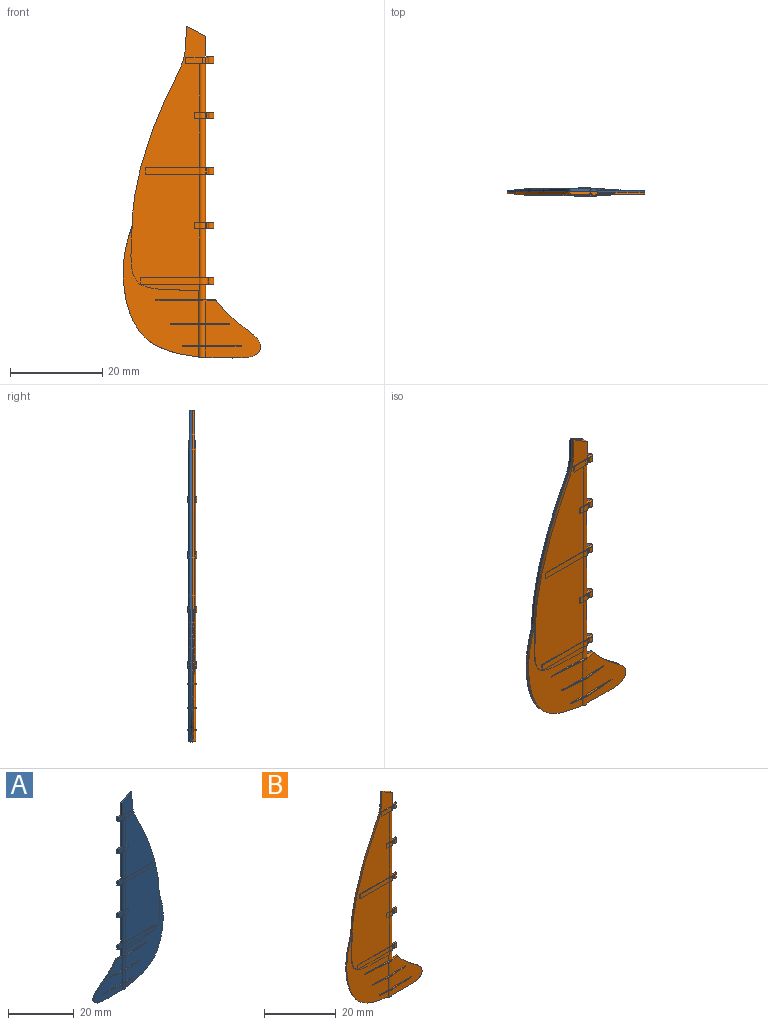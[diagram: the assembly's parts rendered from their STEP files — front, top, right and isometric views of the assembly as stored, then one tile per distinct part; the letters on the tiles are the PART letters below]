
ASSEMBLY  parts=2 mates=1
PART A: 77 faces, bbox 30.6x1x72.1 mm
  f0: plane 4.5x0.6mm, normal (-1,0,0), area 2.7mm2, adj f7,f12,f39,f73
  f1: plane 28.83x17.51mm, normal (0,-1,0), area 202.8mm2, adj f2,f4,f8,f10,f11,f13,f16,f17
  f2: cylinder r=0.79mm len=2.28mm, axis (0,0,1), area 3.8mm2, adj f1,f3,f11,f12,f14,f67
  f3: plane 13.22x13.04mm, normal (0,-1,0), area 99mm2, adj f2,f4,f13,f14,f15,f17,f18,f62
  f4: cylinder r=0.79mm len=4.59mm, axis (0,0,1), area 7.5mm2, adj f1,f3,f62,f68
  f5: cylinder r=0.99mm len=1.4mm, axis (0,0,1), area 2.1mm2, adj f46,f47,f50,f59
  f6: cylinder r=0.99mm len=1.4mm, axis (0,0,1), area 2.1mm2, adj f48,f49,f54,f56
  f7: plane 57.26x16.41mm, normal (0,-1,0), area 557.2mm2, adj f0,f8,f9,f10,f21,f27,f30,f31
  f8: cylinder r=0.79mm len=3.37mm, axis (0,0,1), area 6.6mm2, adj f1,f7,f10,f12,f16,f21
  f9: plane 15.77x0.99mm, normal (0,0,1), area 4mm2, adj f7,f12,f22,f23,f24,f25,f26,f27
  f10: extruded ~14.86x14mm, area 5.2mm2, adj f1,f7,f8,f40
  f11: extruded ~28.36x16.35mm, area 15.2mm2, adj f1,f2,f12,f40
  f12: plane 72.1x30.59mm, normal (0,1,0), area 1005.3mm2, adj f0,f2,f8,f9,f11,f14,f15,f16
  f13: cylinder r=0.79mm len=4.99mm, axis (0,0,1), area 8.1mm2, adj f1,f3,f17,f63
  f14: plane 1.46x0.79mm, normal (0,0,-1), area 0.8mm2, adj f2,f3,f12,f15
  f15: extruded ~12.61x12.32mm, area 11.2mm2, adj f3,f12,f14,f16
  f16: plane 12.82x0.99mm, normal (0,0,1), area 4.3mm2, adj f1,f8,f12,f15,f18,f19,f20
  f17: plane 12.82x0.59mm, normal (0,0,-1), area 3.4mm2, adj f1,f3,f13,f18,f19,f20
  f18: plane 2.67x0.57mm, normal (-0.21,-0.98,0), area 0.5mm2, adj f3,f16,f17,f19
  f19: cylinder r=0.99mm len=0.26mm, axis (0,0,1), area 0.1mm2, adj f16,f17,f18,f20
  f20: plane 9.89x0.59mm, normal (0.06,-1,0), area 2mm2, adj f1,f16,f17,f19
  f21: plane 15.77x0.99mm, normal (0,0,-1), area 4mm2, adj f7,f8,f12,f22,f23,f24,f25,f26
  f22: plane 1.4x0.01mm, normal (1,0,0), area 0mm2, adj f9,f21,f23,f25
  f23: plane 1.4x0.47mm, normal (0,-1,0), area 0.7mm2, adj f9,f21,f22,f24
  f24: cylinder r=0.79mm len=1.4mm, axis (0,0,1), area 2.5mm2, adj f9,f12,f21,f23
  f25: cylinder r=0.99mm len=1.4mm, axis (0,0,1), area 2.1mm2, adj f9,f21,f22,f26
  f26: plane 12.64x1.4mm, normal (0,-1,0), area 17.7mm2, adj f9,f21,f25,f27
  f27: plane 1.4x0.2mm, normal (1,0,0), area 0.3mm2, adj f7,f9,f21,f26
  f28: plane 1.4x0.01mm, normal (1,0,0), area 0mm2, adj f29,f30,f31,f33
  f29: plane 1.4x0.47mm, normal (0,-1,0), area 0.7mm2, adj f28,f30,f31,f32
  f30: plane 4.25x0.99mm, normal (0,0,1), area 1.7mm2, adj f7,f12,f28,f29,f32,f33,f35,f52
  f31: plane 4.25x0.99mm, normal (0,0,-1), area 1.7mm2, adj f7,f12,f28,f29,f32,f33,f36,f52
  f32: cylinder r=0.79mm len=1.4mm, axis (0,0,-1), area 2.5mm2, adj f12,f29,f30,f31
  f33: cylinder r=0.99mm len=1.4mm, axis (0,0,1), area 2.1mm2, adj f28,f30,f31,f52
  f34: cylinder r=0.79mm len=10.59mm, axis (0,0,1), area 19mm2, adj f7,f12,f47,f48
  f35: cylinder r=0.79mm len=10.44mm, axis (0,0,1), area 18.7mm2, adj f7,f12,f30,f46
  f36: cylinder r=0.79mm len=10.58mm, axis (0,0,1), area 18.9mm2, adj f7,f9,f12,f31
  f37: cylinder r=0.79mm len=10.57mm, axis (0,0,1), area 18.9mm2, adj f7,f12,f38,f41,f43,f49
  f38: plane 2.56x0.8mm, normal (0,0,-1), area 1.2mm2, adj f12,f37,f41,f45,f72,f75,f76
  f39: plane 4.12x2.22mm, normal (-0.47,0,0.88), area 2.8mm2, adj f0,f7,f12,f40
  f40: extruded ~43.25x11.74mm, area 27.2mm2, adj f7,f10,f11,f12,f39
  f41: plane 0.01x0.01mm, normal (-1,0,0), area 0mm2, adj f37,f38,f43,f45
  f42: plane 4.3x0.2mm, normal (0,0,1), area 0.8mm2, adj f7,f44,f45,f76
  f43: plane 3.54x0.2mm, normal (0,0,-1), area 0.6mm2, adj f7,f37,f41,f44,f45
  f44: plane 1.4x0.2mm, normal (1,0,0), area 0.3mm2, adj f7,f42,f43,f45
  f45: plane 3.64x1.4mm, normal (0,-1,0), area 5.1mm2, adj f38,f41,f42,f43,f44,f76
  f46: plane 14.77x0.99mm, normal (0,0,-1), area 3.8mm2, adj f5,f7,f12,f35,f50,f51,f59,f60
  f47: plane 14.77x0.99mm, normal (0,0,1), area 3.8mm2, adj f5,f7,f12,f34,f50,f51,f59,f60
  f48: plane 4.27x0.99mm, normal (0,0,-1), area 1.7mm2, adj f6,f7,f12,f34,f54,f55,f56,f57
  f49: plane 4.27x0.99mm, normal (0,0,1), area 1.7mm2, adj f6,f7,f12,f37,f54,f55,f56,f57
  f50: plane 11.63x1.4mm, normal (0,-1,0), area 16.3mm2, adj f5,f46,f47,f51
  f51: plane 1.4x0.2mm, normal (1,0,0), area 0.3mm2, adj f7,f46,f47,f50
  f52: plane 1.4x1.11mm, normal (0,-1,0), area 1.6mm2, adj f30,f31,f33,f53
  f53: plane 1.4x0.2mm, normal (1,0,0), area 0.3mm2, adj f7,f30,f31,f52
  f54: plane 1.4x1.13mm, normal (0,-1,0), area 1.6mm2, adj f6,f48,f49,f55
  f55: plane 1.4x0.2mm, normal (1,0,0), area 0.3mm2, adj f7,f48,f49,f54
  f56: plane 1.4x0.01mm, normal (1,0,0), area 0mm2, adj f6,f48,f49,f57
  f57: plane 1.4x0.47mm, normal (0,-1,0), area 0.7mm2, adj f48,f49,f56,f58
  f58: cylinder r=0.79mm len=1.4mm, axis (0,0,-1), area 2.5mm2, adj f12,f48,f49,f57
  f59: plane 1.4x0.01mm, normal (1,0,0), area 0mm2, adj f5,f46,f47,f60
  f60: plane 1.4x0.47mm, normal (0,-1,0), area 0.7mm2, adj f46,f47,f59,f61
  f61: cylinder r=0.79mm len=1.4mm, axis (0,0,-1), area 2.5mm2, adj f12,f46,f47,f60
  f62: plane 12.84x0.59mm, normal (0,0,-1), area 3.4mm2, adj f1,f3,f4,f64,f65,f66
  f63: plane 12.84x0.59mm, normal (0,0,1), area 3.4mm2, adj f1,f3,f13,f64,f65,f66
  f64: plane 6.75x0.58mm, normal (0.09,-1,0), area 1.4mm2, adj f1,f62,f63,f66
  f65: plane 5.91x0.58mm, normal (-0.1,-1,0), area 1.2mm2, adj f3,f62,f63,f66
  f66: cylinder r=0.99mm len=0.2mm, axis (0,0,1), area 0mm2, adj f62,f63,f64,f65
  f67: plane 12.74x0.59mm, normal (0,0,-1), area 3.4mm2, adj f1,f2,f3,f69,f70,f71
  f68: plane 12.74x0.59mm, normal (0,0,1), area 3.4mm2, adj f1,f3,f4,f69,f70,f71
  f69: plane 8.41x0.58mm, normal (-0.07,-1,0), area 1.7mm2, adj f3,f67,f68,f70
  f70: cylinder r=0.99mm len=0.21mm, axis (0,0,1), area 0mm2, adj f67,f68,f69,f71
  f71: plane 4.13x0.58mm, normal (0.14,-0.99,0), area 0.8mm2, adj f1,f67,f68,f70
  f72: plane 1.39x0.51mm, normal (0,-1,0), area 0.7mm2, adj f38,f73,f75,f76
  f73: plane 0.6x0.51mm, normal (0,0,1), area 0.2mm2, adj f0,f12,f72,f75
  f74: plane 1.57x0.79mm, normal (0,0,1), area 1mm2, adj f12,f75
  f75: cylinder r=0.79mm len=1.57mm, axis (0,0,-1), area 2.5mm2, adj f12,f38,f72,f73,f74
  f76: cylinder r=1.2mm len=1.39mm, axis (0,0,-1), area 1mm2, adj f38,f42,f45,f72
PART B: 81 faces, bbox 30.6x1x72.1 mm
  f0: plane 4.5x0.6mm, normal (1,0,0), area 2.7mm2, adj f7,f12,f36,f68
  f1: plane 28.83x17.51mm, normal (0,-1,0), area 202.8mm2, adj f2,f4,f8,f10,f11,f13,f16,f17
  f2: cylinder r=0.79mm len=2.28mm, axis (0,0,1), area 3.8mm2, adj f1,f3,f11,f12,f14,f62
  f3: plane 13.22x13.04mm, normal (0,-1,0), area 99mm2, adj f2,f4,f13,f14,f15,f17,f18,f57
  f4: cylinder r=0.79mm len=4.59mm, axis (0,0,1), area 7.5mm2, adj f1,f3,f57,f63
  f5: cylinder r=0.99mm len=1.4mm, axis (0,0,1), area 1.9mm2, adj f43,f44,f47,f74
  f6: cylinder r=0.99mm len=1.4mm, axis (0,0,1), area 1.9mm2, adj f45,f46,f51,f75
  f7: plane 57.26x16.41mm, normal (0,-1,0), area 557.2mm2, adj f0,f8,f9,f10,f21,f25,f27,f28
  f8: cylinder r=0.79mm len=3.37mm, axis (0,0,1), area 6.6mm2, adj f1,f7,f10,f12,f16,f21
  f9: plane 15.77x0.99mm, normal (0,0,1), area 4mm2, adj f7,f12,f22,f23,f24,f25,f33,f72
  f10: extruded ~14.86x14mm, area 5.2mm2, adj f1,f7,f8,f37
  f11: extruded ~28.36x16.35mm, area 15.2mm2, adj f1,f2,f12,f37
  f12: plane 72.1x30.59mm, normal (0,1,0), area 1005.3mm2, adj f0,f2,f8,f9,f11,f14,f15,f16
  f13: cylinder r=0.79mm len=4.99mm, axis (0,0,1), area 8.1mm2, adj f1,f3,f17,f58
  f14: plane 1.46x0.79mm, normal (0,0,-1), area 0.8mm2, adj f2,f3,f12,f15
  f15: extruded ~12.61x12.32mm, area 11.2mm2, adj f3,f12,f14,f16
  f16: plane 12.82x0.99mm, normal (0,0,1), area 4.3mm2, adj f1,f8,f12,f15,f18,f19,f20
  f17: plane 12.82x0.59mm, normal (0,0,-1), area 3.4mm2, adj f1,f3,f13,f18,f19,f20
  f18: plane 2.67x0.57mm, normal (0.21,-0.98,0), area 0.5mm2, adj f3,f16,f17,f19
  f19: cylinder r=0.99mm len=0.26mm, axis (0,0,1), area 0.1mm2, adj f16,f17,f18,f20
  f20: plane 9.89x0.59mm, normal (-0.06,-1,0), area 2mm2, adj f1,f16,f17,f19
  f21: plane 15.77x0.99mm, normal (0,0,-1), area 4mm2, adj f7,f8,f12,f22,f23,f24,f25,f72
  f22: cylinder r=0.79mm len=1.4mm, axis (0,0,1), area 2.2mm2, adj f9,f12,f21,f72
  f23: cylinder r=0.99mm len=1.4mm, axis (0,0,1), area 1.7mm2, adj f9,f21,f24,f73
  f24: plane 12.64x1.4mm, normal (0,-1,0), area 17.7mm2, adj f9,f21,f23,f25
  f25: plane 1.4x0.2mm, normal (-1,0,0), area 0.3mm2, adj f7,f9,f21,f24
  f26: plane 1.4x0.11mm, normal (0,-1,0), area 0.1mm2, adj f27,f28,f76,f77
  f27: plane 4.25x0.99mm, normal (0,0,1), area 1.7mm2, adj f7,f12,f26,f29,f30,f32,f49,f50
  f28: plane 4.25x0.99mm, normal (0,0,-1), area 1.7mm2, adj f7,f12,f26,f29,f30,f33,f49,f50
  f29: cylinder r=0.79mm len=1.4mm, axis (0,0,-1), area 2.3mm2, adj f12,f27,f28,f77
  f30: cylinder r=0.99mm len=1.4mm, axis (0,0,1), area 1.9mm2, adj f27,f28,f49,f76
  f31: cylinder r=0.79mm len=10.59mm, axis (0,0,1), area 19mm2, adj f7,f12,f44,f45
  f32: cylinder r=0.79mm len=10.44mm, axis (0,0,1), area 18.7mm2, adj f7,f12,f27,f43
  f33: cylinder r=0.79mm len=10.58mm, axis (0,0,1), area 18.9mm2, adj f7,f9,f12,f28
  f34: cylinder r=0.79mm len=10.57mm, axis (0,0,1), area 18.9mm2, adj f7,f12,f35,f38,f40,f46
  f35: plane 2.56x0.8mm, normal (0,0,-1), area 1.2mm2, adj f12,f34,f38,f42,f67,f70,f71,f80
  f36: plane 4.12x2.22mm, normal (0.47,0,0.88), area 2.8mm2, adj f0,f7,f12,f37
  f37: extruded ~43.25x11.74mm, area 27.2mm2, adj f7,f10,f11,f12,f36
  f38: plane 0.01x0.01mm, normal (1,0,0), area 0mm2, adj f34,f35,f40,f42
  f39: plane 4.3x0.2mm, normal (0,0,1), area 0.8mm2, adj f7,f41,f42,f71
  f40: plane 3.54x0.2mm, normal (0,0,-1), area 0.6mm2, adj f7,f34,f38,f41,f42
  f41: plane 1.4x0.2mm, normal (-1,0,0), area 0.3mm2, adj f7,f39,f40,f42
  f42: plane 3.64x1.4mm, normal (0,-1,0), area 5.1mm2, adj f35,f38,f39,f40,f41,f71
  f43: plane 14.77x0.99mm, normal (0,0,-1), area 3.8mm2, adj f5,f7,f12,f32,f47,f48,f55,f56
  f44: plane 14.77x0.99mm, normal (0,0,1), area 3.8mm2, adj f5,f7,f12,f31,f47,f48,f55,f56
  f45: plane 4.27x0.99mm, normal (0,0,-1), area 1.7mm2, adj f6,f7,f12,f31,f51,f52,f53,f54
  f46: plane 4.27x0.99mm, normal (0,0,1), area 1.7mm2, adj f6,f7,f12,f34,f51,f52,f53,f54
  f47: plane 11.63x1.4mm, normal (0,-1,0), area 16.3mm2, adj f5,f43,f44,f48
  f48: plane 1.4x0.2mm, normal (-1,0,0), area 0.3mm2, adj f7,f43,f44,f47
  f49: plane 1.4x1.11mm, normal (0,-1,0), area 1.6mm2, adj f27,f28,f30,f50
  f50: plane 1.4x0.2mm, normal (-1,0,0), area 0.3mm2, adj f7,f27,f28,f49
  f51: plane 1.4x1.13mm, normal (0,-1,0), area 1.6mm2, adj f6,f45,f46,f52
  f52: plane 1.4x0.2mm, normal (-1,0,0), area 0.3mm2, adj f7,f45,f46,f51
  f53: plane 1.4x0.11mm, normal (0,-1,0), area 0.1mm2, adj f45,f46,f75,f78
  f54: cylinder r=0.79mm len=1.4mm, axis (0,0,-1), area 2.3mm2, adj f12,f45,f46,f78
  f55: plane 1.4x0.11mm, normal (0,-1,0), area 0.1mm2, adj f43,f44,f74,f79
  f56: cylinder r=0.79mm len=1.4mm, axis (0,0,-1), area 2.3mm2, adj f12,f43,f44,f79
  f57: plane 12.84x0.59mm, normal (0,0,-1), area 3.4mm2, adj f1,f3,f4,f59,f60,f61
  f58: plane 12.84x0.59mm, normal (0,0,1), area 3.4mm2, adj f1,f3,f13,f59,f60,f61
  f59: plane 6.75x0.58mm, normal (-0.09,-1,0), area 1.4mm2, adj f1,f57,f58,f61
  f60: plane 5.91x0.58mm, normal (0.1,-1,0), area 1.2mm2, adj f3,f57,f58,f61
  f61: cylinder r=0.99mm len=0.2mm, axis (0,0,1), area 0mm2, adj f57,f58,f59,f60
  f62: plane 12.74x0.59mm, normal (0,0,-1), area 3.4mm2, adj f1,f2,f3,f64,f65,f66
  f63: plane 12.74x0.59mm, normal (0,0,1), area 3.4mm2, adj f1,f3,f4,f64,f65,f66
  f64: plane 8.41x0.58mm, normal (0.07,-1,0), area 1.7mm2, adj f3,f62,f63,f65
  f65: cylinder r=0.99mm len=0.21mm, axis (0,0,1), area 0mm2, adj f62,f63,f64,f66
  f66: plane 4.13x0.58mm, normal (-0.14,-0.99,0), area 0.8mm2, adj f1,f62,f63,f65
  f67: plane 1.39x0.35mm, normal (0,-1,0), area 0.5mm2, adj f35,f68,f71,f80
  f68: plane 0.67x0.61mm, normal (0,0,1), area 0.2mm2, adj f0,f12,f67,f70,f80
  f69: plane 1.57x0.79mm, normal (0,0,1), area 1mm2, adj f12,f70
  f70: cylinder r=0.79mm len=1.57mm, axis (0,0,-1), area 2.3mm2, adj f12,f35,f68,f69,f80
  f71: cylinder r=1.2mm len=1.39mm, axis (0,0,-1), area 1mm2, adj f35,f39,f42,f67
  f72: cylinder r=1mm len=1.4mm, axis (0,0,1), area 0.5mm2, adj f9,f21,f22,f73
  f73: cylinder r=1mm len=1.4mm, axis (0,0,1), area 0.7mm2, adj f9,f21,f23,f72
  f74: cylinder r=0.5mm len=1.4mm, axis (0,0,1), area 0.5mm2, adj f5,f43,f44,f55
  f75: cylinder r=0.5mm len=1.4mm, axis (0,0,1), area 0.5mm2, adj f6,f45,f46,f53
  f76: cylinder r=0.5mm len=1.4mm, axis (0,0,1), area 0.5mm2, adj f26,f27,f28,f30
  f77: cylinder r=0.5mm len=1.4mm, axis (0,0,-1), area 0.4mm2, adj f26,f27,f28,f29
  f78: cylinder r=0.5mm len=1.4mm, axis (0,0,-1), area 0.4mm2, adj f45,f46,f53,f54
  f79: cylinder r=0.5mm len=1.4mm, axis (0,0,-1), area 0.4mm2, adj f43,f44,f55,f56
  f80: cylinder r=0.5mm len=1.39mm, axis (0,0,-1), area 0.4mm2, adj f35,f67,f68,f70
PLACE A rot(axis=(0,0,1),180deg) t=(-35.41,-0.2,-1.29)mm
PLACE B t=(-14.61,-0.2,-1.29)mm
MATE fastened A.f12 <-> B.f12  axis (0,-1,0) through (-43.93,-0.2,-15.08)mm
